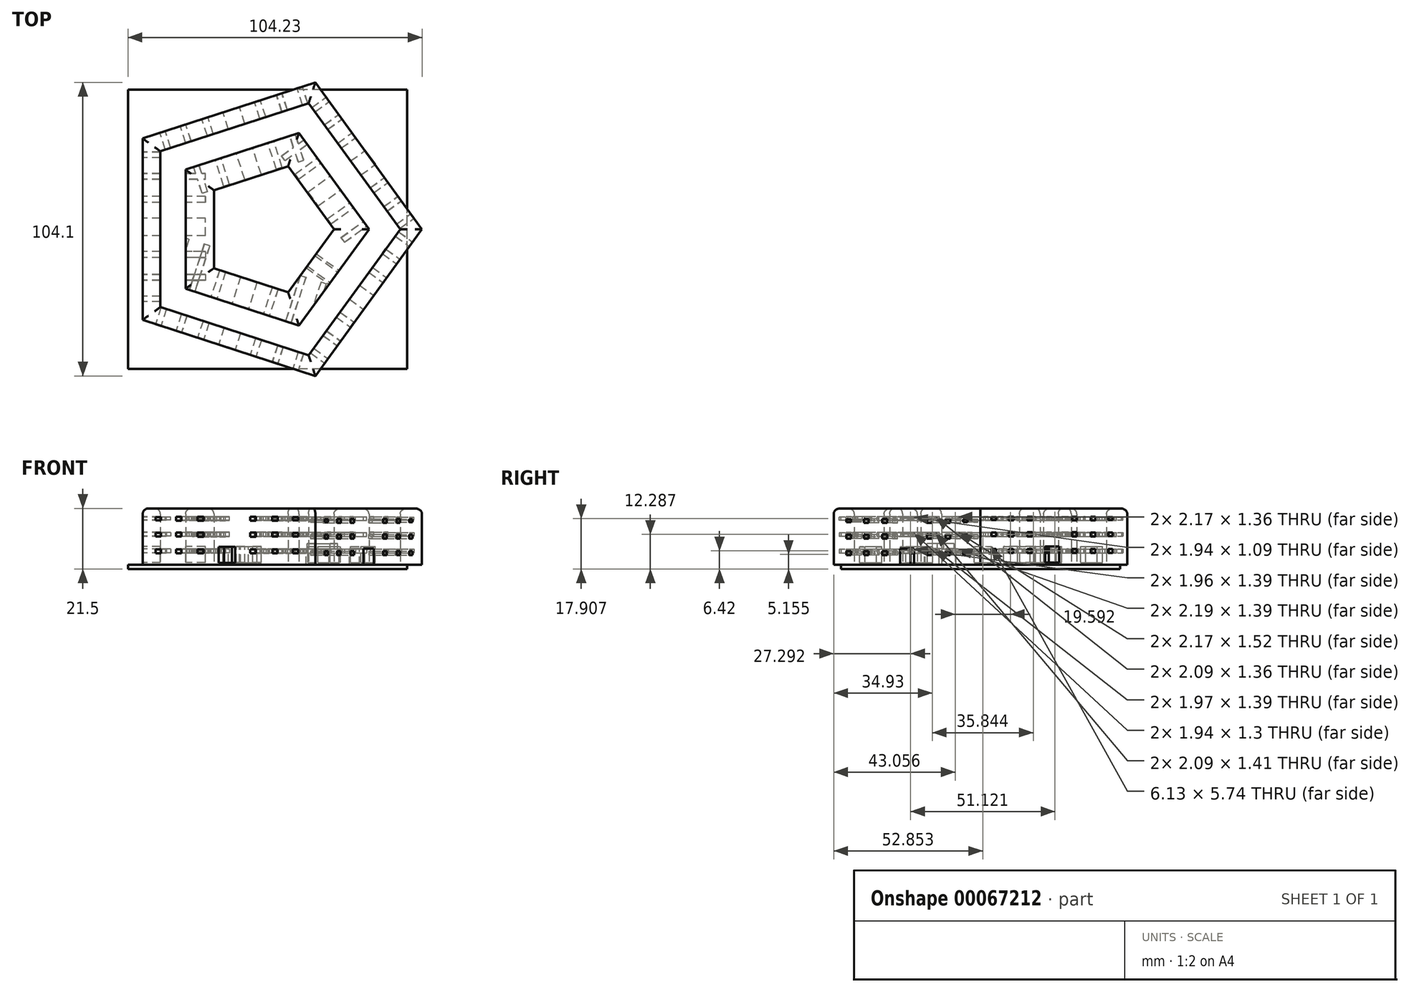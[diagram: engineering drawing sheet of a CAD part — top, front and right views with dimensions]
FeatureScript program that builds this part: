
annotation { "Feature Type Name" : "Feature", "Feature Type Description" : "" }
export const myFeature = defineFeature(function(context is Context, id is Id, definition is map)
    precondition{}
    {
        {
            var Q0;
            Q0=qCreatedBy(makeId("Top.planeOp"),FACE);
            var sketch = newSketch(context, id + "F0", { "sketchPlane" : qUnion([Q0])});
            skCircle(sketch, "E0.cCircle", {"center": v(0, 0) * mm, "radius": 46.99 * mm});
            skLineSegment(sketch, "E0.0", {"start": v(46.99, 0) * mm, "end": v(14.52, -44.69) * mm});
            skLineSegment(sketch, "E0.1", {"start": v(14.52, -44.69) * mm, "end": v(-38.01, -27.62) * mm});
            skLineSegment(sketch, "E0.2", {"start": v(-38.01, -27.62) * mm, "end": v(-38.01, 27.62) * mm});
            skLineSegment(sketch, "E0.3", {"start": v(-38.01, 27.62) * mm, "end": v(14.52, 44.69) * mm});
            skLineSegment(sketch, "E0.4", {"start": v(14.52, 44.69) * mm, "end": v(46.99, 0) * mm});
            skCircle(sketch, "E1.cCircle", {"center": v(0, 0) * mm, "radius": 35.93 * mm, "construction": true});
            skLineSegment(sketch, "E1.0", {"start": v(35.93, 0) * mm, "end": v(11.1, -34.17) * mm});
            skLineSegment(sketch, "E1.1", {"start": v(11.1, -34.17) * mm, "end": v(-29.07, -21.12) * mm});
            skLineSegment(sketch, "E1.2", {"start": v(-29.07, -21.12) * mm, "end": v(-29.07, 21.12) * mm});
            skLineSegment(sketch, "E1.3", {"start": v(-29.07, 21.12) * mm, "end": v(11.1, 34.17) * mm});
            skLineSegment(sketch, "E1.4", {"start": v(11.1, 34.17) * mm, "end": v(35.93, 0) * mm});
            skCircle(sketch, "E2.cCircle", {"center": v(0, 0) * mm, "radius": 23.52 * mm, "construction": true});
            skPoint(sketch, "E2.cCircle.perimeterSnap0", {"position": v(23.52, -17.09) * mm});
            skLineSegment(sketch, "E2.0", {"start": v(23.52, 0) * mm, "end": v(7.27, -22.37) * mm});
            skPoint(sketch, "E2.0.startSnap0", {"position": v(23.52, -17.09) * mm});
            skLineSegment(sketch, "E2.1", {"start": v(7.27, -22.37) * mm, "end": v(-19.03, -13.82) * mm});
            skLineSegment(sketch, "E2.2", {"start": v(-19.03, -13.82) * mm, "end": v(-19.03, 13.82) * mm});
            skLineSegment(sketch, "E2.3", {"start": v(-19.03, 13.82) * mm, "end": v(7.27, 22.37) * mm});
            skLineSegment(sketch, "E2.4", {"start": v(7.27, 22.37) * mm, "end": v(23.52, 0) * mm});
            skCircle(sketch, "E3.cCircle", {"center": v(0, 0) * mm, "radius": 54.73 * mm, "construction": true});
            skLineSegment(sketch, "E3.0", {"start": v(54.73, 0) * mm, "end": v(16.91, -52.05) * mm});
            skLineSegment(sketch, "E3.1", {"start": v(16.91, -52.05) * mm, "end": v(-44.27, -32.17) * mm});
            skLineSegment(sketch, "E3.2", {"start": v(-44.27, -32.17) * mm, "end": v(-44.27, 32.17) * mm});
            skLineSegment(sketch, "E3.3", {"start": v(-44.27, 32.17) * mm, "end": v(16.91, 52.05) * mm});
            skLineSegment(sketch, "E3.4", {"start": v(16.91, 52.05) * mm, "end": v(54.73, 0) * mm});
            skSolve(sketch);
        }
        {
            var Q0;
            Q0=makeQuery(id+"F0.imprint","IMPRINT",FACE,{"disambiguationData":[TD([[makeQuery(id+"F0.imprint","IMPRINT",EDGE,{"derivedFrom":sQuery(id+"F0.wireOp",EDGE,"E1.0")}),-1.0]])]});
            var Q1;
            {var subQ0=sQuery(id+"F0.wireOp",EDGE,"E0.0");Q1=makeQuery(id+"F0.imprint","IMPRINT",FACE,{"disambiguationData":[TD([[makeQuery(id+"F0.imprint","IMPRINT",EDGE,{"derivedFrom":subQ0}),1.0]])]});}
            var Q2;
            {var subQ2=sQuery(id+"F0.wireOp",EDGE,"E3.4");var subQ4=sQuery(id+"F0.wireOp",EDGE,"E3.0");var subQ6=makeQuery(id+"F0.imprint","INTERSECT",VERTEX,{"derivedFrom":[subQ4,subQ2]});Q2=makeQuery(id+"F0.imprint","IMPRINT",FACE,{"disambiguationData":[TD([[makeQuery(id+"F0.imprint","IMPRINT",EDGE,{"disambiguationData":[TD([[subQ6,-1.0]])],"derivedFrom":subQ4}),-1.0]])]});}
            var Q3;
            {var subQ0=sQuery(id+"F0.wireOp",EDGE,"E0.4");Q3=makeQuery(id+"F0.imprint","IMPRINT",FACE,{"disambiguationData":[TD([[makeQuery(id+"F0.imprint","IMPRINT",EDGE,{"derivedFrom":subQ0}),1.0]])]});}
            var Q4;
            {var subQ2=sQuery(id+"F0.wireOp",EDGE,"E3.4");var subQ4=sQuery(id+"F0.wireOp",EDGE,"E3.3");var subQ6=makeQuery(id+"F0.imprint","INTERSECT",VERTEX,{"derivedFrom":[subQ4,subQ2]});Q4=makeQuery(id+"F0.imprint","IMPRINT",FACE,{"disambiguationData":[TD([[makeQuery(id+"F0.imprint","IMPRINT",EDGE,{"disambiguationData":[TD([[subQ6,1.0]])],"derivedFrom":subQ4}),-1.0]])]});}
            var Q5;
            {var subQ0=sQuery(id+"F0.wireOp",EDGE,"E0.3");Q5=makeQuery(id+"F0.imprint","IMPRINT",FACE,{"disambiguationData":[TD([[makeQuery(id+"F0.imprint","IMPRINT",EDGE,{"derivedFrom":subQ0}),1.0]])]});}
            var Q6;
            {var subQ0=sQuery(id+"F0.wireOp",EDGE,"E0.2");Q6=makeQuery(id+"F0.imprint","IMPRINT",FACE,{"disambiguationData":[TD([[makeQuery(id+"F0.imprint","IMPRINT",EDGE,{"derivedFrom":subQ0}),1.0]])]});}
            var Q7;
            {var subQ2=sQuery(id+"F0.wireOp",EDGE,"E3.3");var subQ4=sQuery(id+"F0.wireOp",EDGE,"E3.2");var subQ6=makeQuery(id+"F0.imprint","INTERSECT",VERTEX,{"derivedFrom":[subQ4,subQ2]});Q7=makeQuery(id+"F0.imprint","IMPRINT",FACE,{"disambiguationData":[TD([[makeQuery(id+"F0.imprint","IMPRINT",EDGE,{"disambiguationData":[TD([[subQ6,1.0]])],"derivedFrom":subQ4}),-1.0]])]});}
            var Q8;
            {var subQ0=sQuery(id+"F0.wireOp",EDGE,"E0.1");Q8=makeQuery(id+"F0.imprint","IMPRINT",FACE,{"disambiguationData":[TD([[makeQuery(id+"F0.imprint","IMPRINT",EDGE,{"derivedFrom":subQ0}),1.0]])]});}
            var Q9;
            {var subQ2=sQuery(id+"F0.wireOp",EDGE,"E3.1");var subQ4=sQuery(id+"F0.wireOp",EDGE,"E3.0");var subQ6=makeQuery(id+"F0.imprint","INTERSECT",VERTEX,{"derivedFrom":[subQ4,subQ2]});Q9=makeQuery(id+"F0.imprint","IMPRINT",FACE,{"disambiguationData":[TD([[makeQuery(id+"F0.imprint","IMPRINT",EDGE,{"disambiguationData":[TD([[subQ6,1.0]])],"derivedFrom":subQ4}),-1.0]])]});}
            var Q10;
            {var subQ2=sQuery(id+"F0.wireOp",EDGE,"E3.2");var subQ4=sQuery(id+"F0.wireOp",EDGE,"E3.1");var subQ6=makeQuery(id+"F0.imprint","INTERSECT",VERTEX,{"derivedFrom":[subQ4,subQ2]});Q10=makeQuery(id+"F0.imprint","IMPRINT",FACE,{"disambiguationData":[TD([[makeQuery(id+"F0.imprint","IMPRINT",EDGE,{"disambiguationData":[TD([[subQ6,1.0]])],"derivedFrom":subQ4}),-1.0]])]});}
            extrude(context, id + "F1", {"entities" : qUnion([Q0, Q1, Q2, Q3, Q4, Q5, Q6, Q7, Q8, Q9, Q10]), "depth" : 20 * mm});
        }
        {
            var Q0;
            Q0=makeQuery(id+"F1.opExtrude","SWEPT_FACE",FACE,{"disambiguationData":[OSD([sQuery(id+"F0.wireOp",EDGE,"E3.0")])]});
            var sketch = newSketch(context, id + "F2", { "sketchPlane" : qUnion([Q0])});
            skLineSegment(sketch, "E4.bottom", {"start": v(0, 0) * mm, "end": v(-3.07, 0) * mm});
            skLineSegment(sketch, "E4.top", {"start": v(0, 5.74) * mm, "end": v(-3.07, 5.74) * mm});
            skLineSegment(sketch, "E4.left", {"start": v(0, 0) * mm, "end": v(0, 5.74) * mm});
            skLineSegment(sketch, "E4.right", {"start": v(-3.07, 0) * mm, "end": v(-3.07, 5.74) * mm});
            skLineSegment(sketch, "E5.rect.bottom", {"start": v(-24.6, 15.07) * mm, "end": v(-26.53, 15.07) * mm});
            skLineSegment(sketch, "E5.rect.top", {"start": v(-24.6, 16.17) * mm, "end": v(-26.53, 16.17) * mm});
            skLineSegment(sketch, "E5.rect.left", {"start": v(-24.6, 15.07) * mm, "end": v(-24.6, 16.17) * mm});
            skLineSegment(sketch, "E5.rect.right", {"start": v(-26.53, 15.07) * mm, "end": v(-26.53, 16.17) * mm});
            skPoint(sketch, "E5.rect.middle", {"position": v(-25.56, 15.62) * mm});
            skLineSegment(sketch, "E6.rect.bottom", {"start": v(-24.6, 10.65) * mm, "end": v(-26.53, 10.65) * mm});
            skLineSegment(sketch, "E6.rect.top", {"start": v(-24.6, 9.35) * mm, "end": v(-26.53, 9.35) * mm});
            skLineSegment(sketch, "E6.rect.left", {"start": v(-24.6, 10.65) * mm, "end": v(-24.6, 9.35) * mm});
            skLineSegment(sketch, "E6.rect.right", {"start": v(-26.53, 10.65) * mm, "end": v(-26.53, 9.35) * mm});
            skPoint(sketch, "E6.rect.middle", {"position": v(-25.56, 10) * mm});
            skLineSegment(sketch, "E7.rect.bottom", {"start": v(-24.58, 4.83) * mm, "end": v(-26.54, 4.83) * mm});
            skLineSegment(sketch, "E7.rect.top", {"start": v(-24.58, 3.44) * mm, "end": v(-26.54, 3.44) * mm});
            skLineSegment(sketch, "E7.rect.left", {"start": v(-24.58, 4.83) * mm, "end": v(-24.58, 3.44) * mm});
            skLineSegment(sketch, "E7.rect.right", {"start": v(-26.54, 4.83) * mm, "end": v(-26.54, 3.44) * mm});
            skPoint(sketch, "E7.rect.middle", {"position": v(-25.56, 4.13) * mm});
            skLineSegment(sketch, "E8.rect.bottom", {"start": v(-16.94, 4.83) * mm, "end": v(-18.9, 4.83) * mm});
            skLineSegment(sketch, "E8.rect.top", {"start": v(-16.94, 3.44) * mm, "end": v(-18.9, 3.44) * mm});
            skLineSegment(sketch, "E8.rect.left", {"start": v(-16.94, 4.83) * mm, "end": v(-16.94, 3.44) * mm});
            skLineSegment(sketch, "E8.rect.right", {"start": v(-18.9, 4.83) * mm, "end": v(-18.9, 3.44) * mm});
            skPoint(sketch, "E8.rect.middle", {"position": v(-17.92, 4.13) * mm});
            skLineSegment(sketch, "E9.rect.bottom", {"start": v(-16.88, 9.3) * mm, "end": v(-18.97, 9.3) * mm});
            skLineSegment(sketch, "E9.rect.top", {"start": v(-16.88, 10.7) * mm, "end": v(-18.97, 10.7) * mm});
            skLineSegment(sketch, "E9.rect.left", {"start": v(-16.88, 9.3) * mm, "end": v(-16.88, 10.7) * mm});
            skLineSegment(sketch, "E9.rect.right", {"start": v(-18.97, 9.3) * mm, "end": v(-18.97, 10.7) * mm});
            skPoint(sketch, "E9.rect.middle", {"position": v(-17.92, 10) * mm});
            skLineSegment(sketch, "E10.rect.bottom", {"start": v(-16.88, 14.94) * mm, "end": v(-18.97, 14.94) * mm});
            skLineSegment(sketch, "E10.rect.top", {"start": v(-16.88, 16.3) * mm, "end": v(-18.97, 16.3) * mm});
            skLineSegment(sketch, "E10.rect.left", {"start": v(-16.88, 14.94) * mm, "end": v(-16.88, 16.3) * mm});
            skLineSegment(sketch, "E10.rect.right", {"start": v(-18.97, 14.94) * mm, "end": v(-18.97, 16.3) * mm});
            skPoint(sketch, "E10.rect.middle", {"position": v(-17.92, 15.62) * mm});
            skLineSegment(sketch, "E11.rect.bottom", {"start": v(-10.88, 14.94) * mm, "end": v(-8.71, 14.94) * mm});
            skLineSegment(sketch, "E11.rect.top", {"start": v(-10.88, 16.3) * mm, "end": v(-8.71, 16.3) * mm});
            skLineSegment(sketch, "E11.rect.left", {"start": v(-10.88, 14.94) * mm, "end": v(-10.88, 16.3) * mm});
            skLineSegment(sketch, "E11.rect.right", {"start": v(-8.71, 14.94) * mm, "end": v(-8.71, 16.3) * mm});
            skPoint(sketch, "E11.rect.middle", {"position": v(-9.8, 15.62) * mm});
            skLineSegment(sketch, "E12.rect.bottom", {"start": v(-10.88, 9.24) * mm, "end": v(-8.71, 9.24) * mm});
            skLineSegment(sketch, "E12.rect.top", {"start": v(-10.88, 10.76) * mm, "end": v(-8.71, 10.76) * mm});
            skLineSegment(sketch, "E12.rect.left", {"start": v(-10.88, 9.24) * mm, "end": v(-10.88, 10.76) * mm});
            skLineSegment(sketch, "E12.rect.right", {"start": v(-8.71, 9.24) * mm, "end": v(-8.71, 10.76) * mm});
            skPoint(sketch, "E12.rect.middle", {"position": v(-9.8, 10) * mm});
            skLineSegment(sketch, "E13.rect.bottom", {"start": v(-8.7, 4.83) * mm, "end": v(-10.89, 4.83) * mm});
            skLineSegment(sketch, "E13.rect.top", {"start": v(-8.7, 3.44) * mm, "end": v(-10.89, 3.44) * mm});
            skLineSegment(sketch, "E13.rect.left", {"start": v(-8.7, 4.83) * mm, "end": v(-8.7, 3.44) * mm});
            skLineSegment(sketch, "E13.rect.right", {"start": v(-10.89, 4.83) * mm, "end": v(-10.89, 3.44) * mm});
            skPoint(sketch, "E13.rect.middle", {"position": v(-9.8, 4.13) * mm});
            skLineSegment(sketch, "E14.MirrorCS", {"start": v(3.07, 0) * mm, "end": v(3.07, 5.74) * mm});
            skLineSegment(sketch, "E15.MirrorCS", {"start": v(0, 5.74) * mm, "end": v(3.07, 5.74) * mm});
            skLineSegment(sketch, "E16.MirrorCS", {"start": v(8.7, 4.83) * mm, "end": v(8.7, 3.44) * mm});
            skLineSegment(sketch, "E17.MirrorCS", {"start": v(8.7, 4.83) * mm, "end": v(10.89, 4.83) * mm});
            skLineSegment(sketch, "E18.MirrorCS", {"start": v(10.89, 4.83) * mm, "end": v(10.89, 3.44) * mm});
            skLineSegment(sketch, "E19.MirrorCS", {"start": v(8.7, 3.44) * mm, "end": v(10.89, 3.44) * mm});
            skLineSegment(sketch, "E20.MirrorCS", {"start": v(8.71, 9.24) * mm, "end": v(8.71, 10.76) * mm});
            skLineSegment(sketch, "E21.MirrorCS", {"start": v(10.88, 10.76) * mm, "end": v(8.71, 10.76) * mm});
            skLineSegment(sketch, "E22.MirrorCS", {"start": v(10.88, 9.24) * mm, "end": v(10.88, 10.76) * mm});
            skLineSegment(sketch, "E23.MirrorCS", {"start": v(10.88, 9.24) * mm, "end": v(8.71, 9.24) * mm});
            skLineSegment(sketch, "E24.MirrorCS", {"start": v(10.88, 16.3) * mm, "end": v(8.71, 16.3) * mm});
            skLineSegment(sketch, "E25.MirrorCS", {"start": v(8.71, 14.94) * mm, "end": v(8.71, 16.3) * mm});
            skLineSegment(sketch, "E26.MirrorCS", {"start": v(10.88, 14.94) * mm, "end": v(8.71, 14.94) * mm});
            skLineSegment(sketch, "E27.MirrorCS", {"start": v(10.88, 14.94) * mm, "end": v(10.88, 16.3) * mm});
            skLineSegment(sketch, "E28.MirrorCS", {"start": v(16.88, 14.94) * mm, "end": v(16.88, 16.3) * mm});
            skLineSegment(sketch, "E29.MirrorCS", {"start": v(16.88, 16.3) * mm, "end": v(18.97, 16.3) * mm});
            skLineSegment(sketch, "E30.MirrorCS", {"start": v(18.97, 14.94) * mm, "end": v(18.97, 16.3) * mm});
            skLineSegment(sketch, "E31.MirrorCS", {"start": v(16.88, 14.94) * mm, "end": v(18.97, 14.94) * mm});
            skLineSegment(sketch, "E32.MirrorCS", {"start": v(16.88, 10.7) * mm, "end": v(18.97, 10.7) * mm});
            skLineSegment(sketch, "E33.MirrorCS", {"start": v(16.88, 9.3) * mm, "end": v(16.88, 10.7) * mm});
            skLineSegment(sketch, "E34.MirrorCS", {"start": v(16.88, 9.3) * mm, "end": v(18.97, 9.3) * mm});
            skLineSegment(sketch, "E35.MirrorCS", {"start": v(18.97, 9.3) * mm, "end": v(18.97, 10.7) * mm});
            skLineSegment(sketch, "E36.MirrorCS", {"start": v(24.6, 15.07) * mm, "end": v(24.6, 16.17) * mm});
            skPoint(sketch, "E37.MirrorP", {"position": v(25.56, 15.62) * mm});
            skLineSegment(sketch, "E38.MirrorCS", {"start": v(24.6, 16.17) * mm, "end": v(26.53, 16.17) * mm});
            skLineSegment(sketch, "E39.MirrorCS", {"start": v(26.53, 15.07) * mm, "end": v(26.53, 16.17) * mm});
            skLineSegment(sketch, "E40.MirrorCS", {"start": v(24.6, 15.07) * mm, "end": v(26.53, 15.07) * mm});
            skLineSegment(sketch, "E41.MirrorCS", {"start": v(24.6, 10.65) * mm, "end": v(26.53, 10.65) * mm});
            skLineSegment(sketch, "E42.MirrorCS", {"start": v(24.6, 10.65) * mm, "end": v(24.6, 9.35) * mm});
            skLineSegment(sketch, "E43.MirrorCS", {"start": v(24.6, 9.35) * mm, "end": v(26.53, 9.35) * mm});
            skLineSegment(sketch, "E44.MirrorCS", {"start": v(26.53, 10.65) * mm, "end": v(26.53, 9.35) * mm});
            skPoint(sketch, "E45.MirrorP", {"position": v(25.56, 4.13) * mm});
            skPoint(sketch, "E46.MirrorP", {"position": v(17.92, 4.13) * mm});
            skPoint(sketch, "E47.MirrorP", {"position": v(9.8, 4.13) * mm});
            skPoint(sketch, "E48.MirrorP", {"position": v(9.8, 10) * mm});
            skPoint(sketch, "E49.MirrorP", {"position": v(9.8, 15.62) * mm});
            skPoint(sketch, "E50.MirrorP", {"position": v(17.92, 15.62) * mm});
            skPoint(sketch, "E51.MirrorP", {"position": v(17.92, 10) * mm});
            skPoint(sketch, "E52.MirrorP", {"position": v(25.56, 10) * mm});
            skLineSegment(sketch, "E53.MirrorCS", {"start": v(16.94, 4.83) * mm, "end": v(18.9, 4.83) * mm});
            skLineSegment(sketch, "E54.MirrorCS", {"start": v(18.9, 4.83) * mm, "end": v(18.9, 3.44) * mm});
            skLineSegment(sketch, "E55.MirrorCS", {"start": v(16.94, 3.44) * mm, "end": v(18.9, 3.44) * mm});
            skLineSegment(sketch, "E56.MirrorCS", {"start": v(16.94, 4.83) * mm, "end": v(16.94, 3.44) * mm});
            skLineSegment(sketch, "E57.MirrorCS", {"start": v(24.58, 4.83) * mm, "end": v(26.54, 4.83) * mm});
            skLineSegment(sketch, "E58.MirrorCS", {"start": v(26.54, 4.83) * mm, "end": v(26.54, 3.44) * mm});
            skLineSegment(sketch, "E59.MirrorCS", {"start": v(24.58, 3.44) * mm, "end": v(26.54, 3.44) * mm});
            skLineSegment(sketch, "E60.MirrorCS", {"start": v(24.58, 4.83) * mm, "end": v(24.58, 3.44) * mm});
            skSolve(sketch);
        }
        {
            var Q0;
            Q0 = qSketchRegion(id + "F2", true);
            extrude(context, id + "F3", {"entities" : qUnion([Q0]), "operationType" : NewBodyOperationType.REMOVE, "oppositeDirection" : true, "depth" : 15 * mm});
        }
        {
            var Q0;
            {var subQ0=sQuery(id+"F2.wireOp",EDGE,"E4.left");Q0=makeQuery(id+"F2.imprint","IMPRINT",FACE,{"disambiguationData":[TD([[makeQuery(id+"F2.imprint","IMPRINT",EDGE,{"derivedFrom":subQ0}),-1.0]])]});}
            var Q1;
            Q1=makeQuery(id+"F2.imprint","IMPRINT",FACE,{"disambiguationData":[TD([[makeQuery(id+"F2.imprint","IMPRINT",EDGE,{"derivedFrom":sQuery(id+"F2.wireOp",EDGE,"E4.bottom")}),-1.0]])]});
            extrude(context, id + "F4", {"entities" : qUnion([Q0, Q1]), "operationType" : NewBodyOperationType.REMOVE, "oppositeDirection" : true, "depth" : 61.4 * mm});
        }
        {
            var Q0;
            Q0=makeQuery(id+"F1.opExtrude","SWEPT_FACE",FACE,{"disambiguationData":[OSD([sQuery(id+"F0.wireOp",EDGE,"E1.0")])]});
            var sketch = newSketch(context, id + "F5", { "sketchPlane" : qUnion([Q0])});
            skLineSegment(sketch, "E61.bottom", {"start": v(0, 0) * mm, "end": v(-2.3, 0) * mm});
            skLineSegment(sketch, "E61.top", {"start": v(0, 7.45) * mm, "end": v(-2.3, 7.45) * mm});
            skLineSegment(sketch, "E61.left", {"start": v(0, 0) * mm, "end": v(0, 7.45) * mm});
            skLineSegment(sketch, "E61.right", {"start": v(-2.3, 0) * mm, "end": v(-2.3, 7.45) * mm});
            skLineSegment(sketch, "E62.MirrorCS", {"start": v(0, 7.45) * mm, "end": v(2.3, 7.45) * mm});
            skLineSegment(sketch, "E63.MirrorCS", {"start": v(2.3, 0) * mm, "end": v(2.3, 7.45) * mm});
            skLineSegment(sketch, "E64.MirrorCS", {"start": v(0, 0) * mm, "end": v(2.3, 0) * mm});
            skSolve(sketch);
        }
        {
            var Q0;
            Q0 = qSketchRegion(id + "F5", true);
            extrude(context, id + "F6", {"entities" : qUnion([Q0]), "operationType" : NewBodyOperationType.REMOVE, "oppositeDirection" : true, "depth" : 25 * mm});
        }
        {
            var Q0;
            Q0=makeQuery(id+"F1.opExtrude","SWEPT_FACE",FACE,{"disambiguationData":[OSD([sQuery(id+"F0.wireOp",EDGE,"E3.1")])]});
            var sketch = newSketch(context, id + "F7", { "sketchPlane" : qUnion([Q0])});
            skLineSegment(sketch, "E65.bottom", {"start": v(-0.8, 0.7) * mm, "end": v(-3.86, 0.7) * mm});
            skLineSegment(sketch, "E65.top", {"start": v(-0.8, 6.43) * mm, "end": v(-3.86, 6.43) * mm});
            skLineSegment(sketch, "E65.left", {"start": v(-0.8, 0.7) * mm, "end": v(-0.8, 6.43) * mm});
            skLineSegment(sketch, "E65.right", {"start": v(-3.86, 0.7) * mm, "end": v(-3.86, 6.43) * mm});
            skLineSegment(sketch, "E66.rect.bottom", {"start": v(-25.39, 15.77) * mm, "end": v(-27.33, 15.77) * mm});
            skLineSegment(sketch, "E66.rect.top", {"start": v(-25.39, 16.86) * mm, "end": v(-27.33, 16.86) * mm});
            skLineSegment(sketch, "E66.rect.left", {"start": v(-25.39, 15.77) * mm, "end": v(-25.39, 16.86) * mm});
            skLineSegment(sketch, "E66.rect.right", {"start": v(-27.33, 15.77) * mm, "end": v(-27.33, 16.86) * mm});
            skPoint(sketch, "E66.rect.middle", {"position": v(-26.36, 16.32) * mm});
            skLineSegment(sketch, "E67.rect.bottom", {"start": v(-25.39, 11.35) * mm, "end": v(-27.33, 11.35) * mm});
            skLineSegment(sketch, "E67.rect.top", {"start": v(-25.39, 10.05) * mm, "end": v(-27.33, 10.05) * mm});
            skLineSegment(sketch, "E67.rect.left", {"start": v(-25.39, 11.35) * mm, "end": v(-25.39, 10.05) * mm});
            skLineSegment(sketch, "E67.rect.right", {"start": v(-27.33, 11.35) * mm, "end": v(-27.33, 10.05) * mm});
            skPoint(sketch, "E67.rect.middle", {"position": v(-26.36, 10.7) * mm});
            skLineSegment(sketch, "E68.rect.bottom", {"start": v(-25.38, 5.52) * mm, "end": v(-27.34, 5.52) * mm});
            skLineSegment(sketch, "E68.rect.top", {"start": v(-25.38, 4.13) * mm, "end": v(-27.34, 4.13) * mm});
            skLineSegment(sketch, "E68.rect.left", {"start": v(-25.38, 5.52) * mm, "end": v(-25.38, 4.13) * mm});
            skLineSegment(sketch, "E68.rect.right", {"start": v(-27.34, 5.52) * mm, "end": v(-27.34, 4.13) * mm});
            skPoint(sketch, "E68.rect.middle", {"position": v(-26.36, 4.83) * mm});
            skLineSegment(sketch, "E69.rect.bottom", {"start": v(-17.73, 5.52) * mm, "end": v(-19.7, 5.52) * mm});
            skLineSegment(sketch, "E69.rect.top", {"start": v(-17.73, 4.13) * mm, "end": v(-19.7, 4.13) * mm});
            skLineSegment(sketch, "E69.rect.left", {"start": v(-17.73, 5.52) * mm, "end": v(-17.73, 4.13) * mm});
            skLineSegment(sketch, "E69.rect.right", {"start": v(-19.7, 5.52) * mm, "end": v(-19.7, 4.13) * mm});
            skPoint(sketch, "E69.rect.middle", {"position": v(-18.72, 4.83) * mm});
            skLineSegment(sketch, "E70.rect.bottom", {"start": v(-17.67, 10) * mm, "end": v(-19.76, 10) * mm});
            skLineSegment(sketch, "E70.rect.top", {"start": v(-17.67, 11.4) * mm, "end": v(-19.76, 11.4) * mm});
            skLineSegment(sketch, "E70.rect.left", {"start": v(-17.67, 10) * mm, "end": v(-17.67, 11.4) * mm});
            skLineSegment(sketch, "E70.rect.right", {"start": v(-19.76, 10) * mm, "end": v(-19.76, 11.4) * mm});
            skPoint(sketch, "E70.rect.middle", {"position": v(-18.72, 10.7) * mm});
            skLineSegment(sketch, "E71.rect.bottom", {"start": v(-17.67, 15.64) * mm, "end": v(-19.76, 15.64) * mm});
            skLineSegment(sketch, "E71.rect.top", {"start": v(-17.67, 17) * mm, "end": v(-19.76, 17) * mm});
            skLineSegment(sketch, "E71.rect.left", {"start": v(-17.67, 15.64) * mm, "end": v(-17.67, 17) * mm});
            skLineSegment(sketch, "E71.rect.right", {"start": v(-19.76, 15.64) * mm, "end": v(-19.76, 17) * mm});
            skPoint(sketch, "E71.rect.middle", {"position": v(-18.72, 16.32) * mm});
            skLineSegment(sketch, "E72.rect.bottom", {"start": v(-11.67, 15.64) * mm, "end": v(-9.5, 15.64) * mm});
            skLineSegment(sketch, "E72.rect.top", {"start": v(-11.67, 17) * mm, "end": v(-9.5, 17) * mm});
            skLineSegment(sketch, "E72.rect.left", {"start": v(-11.67, 15.64) * mm, "end": v(-11.67, 17) * mm});
            skLineSegment(sketch, "E72.rect.right", {"start": v(-9.5, 15.64) * mm, "end": v(-9.5, 17) * mm});
            skPoint(sketch, "E72.rect.middle", {"position": v(-10.6, 16.32) * mm});
            skLineSegment(sketch, "E73.rect.bottom", {"start": v(-11.67, 9.93) * mm, "end": v(-9.5, 9.93) * mm});
            skLineSegment(sketch, "E73.rect.top", {"start": v(-11.67, 11.46) * mm, "end": v(-9.5, 11.46) * mm});
            skLineSegment(sketch, "E73.rect.left", {"start": v(-11.67, 9.93) * mm, "end": v(-11.67, 11.46) * mm});
            skLineSegment(sketch, "E73.rect.right", {"start": v(-9.5, 9.93) * mm, "end": v(-9.5, 11.46) * mm});
            skPoint(sketch, "E73.rect.middle", {"position": v(-10.6, 10.7) * mm});
            skLineSegment(sketch, "E74.rect.bottom", {"start": v(-9.5, 5.52) * mm, "end": v(-11.68, 5.52) * mm});
            skLineSegment(sketch, "E74.rect.top", {"start": v(-9.5, 4.13) * mm, "end": v(-11.68, 4.13) * mm});
            skLineSegment(sketch, "E74.rect.left", {"start": v(-9.5, 5.52) * mm, "end": v(-9.5, 4.13) * mm});
            skLineSegment(sketch, "E74.rect.right", {"start": v(-11.68, 5.52) * mm, "end": v(-11.68, 4.13) * mm});
            skPoint(sketch, "E74.rect.middle", {"position": v(-10.6, 4.83) * mm});
            skLineSegment(sketch, "E75.MirrorCS", {"start": v(2.27, 0.7) * mm, "end": v(2.27, 6.43) * mm});
            skLineSegment(sketch, "E76.MirrorCS", {"start": v(-0.8, 6.43) * mm, "end": v(2.27, 6.43) * mm});
            skLineSegment(sketch, "E77.MirrorCS", {"start": v(7.9, 5.52) * mm, "end": v(7.9, 4.13) * mm});
            skLineSegment(sketch, "E78.MirrorCS", {"start": v(7.9, 5.52) * mm, "end": v(10.1, 5.52) * mm});
            skLineSegment(sketch, "E79.MirrorCS", {"start": v(10.1, 5.52) * mm, "end": v(10.1, 4.13) * mm});
            skLineSegment(sketch, "E80.MirrorCS", {"start": v(7.9, 4.13) * mm, "end": v(10.1, 4.13) * mm});
            skLineSegment(sketch, "E81.MirrorCS", {"start": v(7.92, 9.93) * mm, "end": v(7.92, 11.46) * mm});
            skLineSegment(sketch, "E82.MirrorCS", {"start": v(10.08, 11.46) * mm, "end": v(7.92, 11.46) * mm});
            skLineSegment(sketch, "E83.MirrorCS", {"start": v(10.08, 9.93) * mm, "end": v(10.08, 11.46) * mm});
            skLineSegment(sketch, "E84.MirrorCS", {"start": v(10.08, 9.93) * mm, "end": v(7.92, 9.93) * mm});
            skLineSegment(sketch, "E85.MirrorCS", {"start": v(10.08, 17) * mm, "end": v(7.92, 17) * mm});
            skLineSegment(sketch, "E86.MirrorCS", {"start": v(7.92, 15.64) * mm, "end": v(7.92, 17) * mm});
            skLineSegment(sketch, "E87.MirrorCS", {"start": v(10.08, 15.64) * mm, "end": v(7.92, 15.64) * mm});
            skLineSegment(sketch, "E88.MirrorCS", {"start": v(10.08, 15.64) * mm, "end": v(10.08, 17) * mm});
            skLineSegment(sketch, "E89.MirrorCS", {"start": v(16.08, 15.64) * mm, "end": v(16.08, 17) * mm});
            skLineSegment(sketch, "E90.MirrorCS", {"start": v(16.08, 17) * mm, "end": v(18.17, 17) * mm});
            skLineSegment(sketch, "E91.MirrorCS", {"start": v(18.17, 15.64) * mm, "end": v(18.17, 17) * mm});
            skLineSegment(sketch, "E92.MirrorCS", {"start": v(16.08, 15.64) * mm, "end": v(18.17, 15.64) * mm});
            skLineSegment(sketch, "E93.MirrorCS", {"start": v(16.08, 11.4) * mm, "end": v(18.17, 11.4) * mm});
            skLineSegment(sketch, "E94.MirrorCS", {"start": v(16.08, 10) * mm, "end": v(16.08, 11.4) * mm});
            skLineSegment(sketch, "E95.MirrorCS", {"start": v(16.08, 10) * mm, "end": v(18.17, 10) * mm});
            skLineSegment(sketch, "E96.MirrorCS", {"start": v(18.17, 10) * mm, "end": v(18.17, 11.4) * mm});
            skLineSegment(sketch, "E97.MirrorCS", {"start": v(23.8, 15.77) * mm, "end": v(23.8, 16.86) * mm});
            skPoint(sketch, "E98.MirrorP", {"position": v(24.77, 16.32) * mm});
            skLineSegment(sketch, "E99.MirrorCS", {"start": v(23.8, 16.86) * mm, "end": v(25.74, 16.86) * mm});
            skLineSegment(sketch, "E100.MirrorCS", {"start": v(25.74, 15.77) * mm, "end": v(25.74, 16.86) * mm});
            skLineSegment(sketch, "E101.MirrorCS", {"start": v(23.8, 15.77) * mm, "end": v(25.74, 15.77) * mm});
            skLineSegment(sketch, "E102.MirrorCS", {"start": v(23.8, 11.35) * mm, "end": v(25.74, 11.35) * mm});
            skLineSegment(sketch, "E103.MirrorCS", {"start": v(23.8, 11.35) * mm, "end": v(23.8, 10.05) * mm});
            skLineSegment(sketch, "E104.MirrorCS", {"start": v(23.8, 10.05) * mm, "end": v(25.74, 10.05) * mm});
            skLineSegment(sketch, "E105.MirrorCS", {"start": v(25.74, 11.35) * mm, "end": v(25.74, 10.05) * mm});
            skPoint(sketch, "E106.MirrorP", {"position": v(24.77, 4.83) * mm});
            skPoint(sketch, "E107.MirrorP", {"position": v(17.13, 4.83) * mm});
            skPoint(sketch, "E108.MirrorP", {"position": v(9, 4.83) * mm});
            skPoint(sketch, "E109.MirrorP", {"position": v(9, 10.7) * mm});
            skPoint(sketch, "E110.MirrorP", {"position": v(9, 16.32) * mm});
            skPoint(sketch, "E111.MirrorP", {"position": v(17.13, 16.32) * mm});
            skPoint(sketch, "E112.MirrorP", {"position": v(17.13, 10.7) * mm});
            skPoint(sketch, "E113.MirrorP", {"position": v(24.77, 10.7) * mm});
            skLineSegment(sketch, "E114.MirrorCS", {"start": v(16.14, 5.52) * mm, "end": v(18.11, 5.52) * mm});
            skLineSegment(sketch, "E115.MirrorCS", {"start": v(18.11, 5.52) * mm, "end": v(18.11, 4.13) * mm});
            skLineSegment(sketch, "E116.MirrorCS", {"start": v(16.14, 4.13) * mm, "end": v(18.11, 4.13) * mm});
            skLineSegment(sketch, "E117.MirrorCS", {"start": v(16.14, 5.52) * mm, "end": v(16.14, 4.13) * mm});
            skLineSegment(sketch, "E118.MirrorCS", {"start": v(23.78, 5.52) * mm, "end": v(25.75, 5.52) * mm});
            skLineSegment(sketch, "E119.MirrorCS", {"start": v(25.75, 5.52) * mm, "end": v(25.75, 4.13) * mm});
            skLineSegment(sketch, "E120.MirrorCS", {"start": v(23.78, 4.13) * mm, "end": v(25.75, 4.13) * mm});
            skLineSegment(sketch, "E121.MirrorCS", {"start": v(23.78, 5.52) * mm, "end": v(23.78, 4.13) * mm});
            skLineSegment(sketch, "E122", {"start": v(2.27, 0.7) * mm, "end": v(-0.8, 0.7) * mm});
            skSolve(sketch);
        }
        {
            var Q0;
            Q0=makeQuery(id+"F1.opExtrude","SWEPT_FACE",FACE,{"disambiguationData":[OSD([sQuery(id+"F0.wireOp",EDGE,"E3.2")])]});
            var sketch = newSketch(context, id + "F8", { "sketchPlane" : qUnion([Q0])});
            skLineSegment(sketch, "E123.bottom", {"start": v(-0.8, 0.79) * mm, "end": v(-3.87, 0.79) * mm});
            skLineSegment(sketch, "E123.top", {"start": v(-0.8, 6.52) * mm, "end": v(-3.87, 6.52) * mm});
            skLineSegment(sketch, "E123.left", {"start": v(-0.8, 0.79) * mm, "end": v(-0.8, 6.52) * mm});
            skLineSegment(sketch, "E123.right", {"start": v(-3.87, 0.79) * mm, "end": v(-3.87, 6.52) * mm});
            skLineSegment(sketch, "E124.rect.bottom", {"start": v(-25.4, 15.86) * mm, "end": v(-27.33, 15.86) * mm});
            skLineSegment(sketch, "E124.rect.top", {"start": v(-25.4, 16.95) * mm, "end": v(-27.33, 16.95) * mm});
            skLineSegment(sketch, "E124.rect.left", {"start": v(-25.4, 15.86) * mm, "end": v(-25.4, 16.95) * mm});
            skLineSegment(sketch, "E124.rect.right", {"start": v(-27.33, 15.86) * mm, "end": v(-27.33, 16.95) * mm});
            skPoint(sketch, "E124.rect.middle", {"position": v(-26.36, 16.4) * mm});
            skLineSegment(sketch, "E125.rect.bottom", {"start": v(-25.4, 11.44) * mm, "end": v(-27.33, 11.44) * mm});
            skLineSegment(sketch, "E125.rect.top", {"start": v(-25.4, 10.14) * mm, "end": v(-27.33, 10.14) * mm});
            skLineSegment(sketch, "E125.rect.left", {"start": v(-25.4, 11.44) * mm, "end": v(-25.4, 10.14) * mm});
            skLineSegment(sketch, "E125.rect.right", {"start": v(-27.33, 11.44) * mm, "end": v(-27.33, 10.14) * mm});
            skPoint(sketch, "E125.rect.middle", {"position": v(-26.36, 10.79) * mm});
            skLineSegment(sketch, "E126.rect.bottom", {"start": v(-25.38, 5.61) * mm, "end": v(-27.34, 5.61) * mm});
            skLineSegment(sketch, "E126.rect.top", {"start": v(-25.38, 4.23) * mm, "end": v(-27.34, 4.23) * mm});
            skLineSegment(sketch, "E126.rect.left", {"start": v(-25.38, 5.61) * mm, "end": v(-25.38, 4.23) * mm});
            skLineSegment(sketch, "E126.rect.right", {"start": v(-27.34, 5.61) * mm, "end": v(-27.34, 4.23) * mm});
            skPoint(sketch, "E126.rect.middle", {"position": v(-26.36, 4.92) * mm});
            skLineSegment(sketch, "E127.rect.bottom", {"start": v(-17.74, 5.61) * mm, "end": v(-19.71, 5.61) * mm});
            skLineSegment(sketch, "E127.rect.top", {"start": v(-17.74, 4.23) * mm, "end": v(-19.71, 4.23) * mm});
            skLineSegment(sketch, "E127.rect.left", {"start": v(-17.74, 5.61) * mm, "end": v(-17.74, 4.23) * mm});
            skLineSegment(sketch, "E127.rect.right", {"start": v(-19.71, 5.61) * mm, "end": v(-19.71, 4.23) * mm});
            skPoint(sketch, "E127.rect.middle", {"position": v(-18.72, 4.92) * mm});
            skLineSegment(sketch, "E128.rect.bottom", {"start": v(-17.68, 10.08) * mm, "end": v(-19.77, 10.08) * mm});
            skLineSegment(sketch, "E128.rect.top", {"start": v(-17.68, 11.5) * mm, "end": v(-19.77, 11.5) * mm});
            skLineSegment(sketch, "E128.rect.left", {"start": v(-17.68, 10.08) * mm, "end": v(-17.68, 11.5) * mm});
            skLineSegment(sketch, "E128.rect.right", {"start": v(-19.77, 10.08) * mm, "end": v(-19.77, 11.5) * mm});
            skPoint(sketch, "E128.rect.middle", {"position": v(-18.72, 10.79) * mm});
            skLineSegment(sketch, "E129.rect.bottom", {"start": v(-17.68, 15.73) * mm, "end": v(-19.77, 15.73) * mm});
            skLineSegment(sketch, "E129.rect.top", {"start": v(-17.68, 17.08) * mm, "end": v(-19.77, 17.08) * mm});
            skLineSegment(sketch, "E129.rect.left", {"start": v(-17.68, 15.73) * mm, "end": v(-17.68, 17.08) * mm});
            skLineSegment(sketch, "E129.rect.right", {"start": v(-19.77, 15.73) * mm, "end": v(-19.77, 17.08) * mm});
            skPoint(sketch, "E129.rect.middle", {"position": v(-18.72, 16.4) * mm});
            skLineSegment(sketch, "E130.rect.bottom", {"start": v(-11.68, 15.73) * mm, "end": v(-9.52, 15.73) * mm});
            skLineSegment(sketch, "E130.rect.top", {"start": v(-11.68, 17.08) * mm, "end": v(-9.52, 17.08) * mm});
            skLineSegment(sketch, "E130.rect.left", {"start": v(-11.68, 15.73) * mm, "end": v(-11.68, 17.08) * mm});
            skLineSegment(sketch, "E130.rect.right", {"start": v(-9.52, 15.73) * mm, "end": v(-9.52, 17.08) * mm});
            skPoint(sketch, "E130.rect.middle", {"position": v(-10.6, 16.4) * mm});
            skLineSegment(sketch, "E131.rect.bottom", {"start": v(-11.68, 10.02) * mm, "end": v(-9.52, 10.02) * mm});
            skLineSegment(sketch, "E131.rect.top", {"start": v(-11.68, 11.55) * mm, "end": v(-9.52, 11.55) * mm});
            skLineSegment(sketch, "E131.rect.left", {"start": v(-11.68, 10.02) * mm, "end": v(-11.68, 11.55) * mm});
            skLineSegment(sketch, "E131.rect.right", {"start": v(-9.52, 10.02) * mm, "end": v(-9.52, 11.55) * mm});
            skPoint(sketch, "E131.rect.middle", {"position": v(-10.6, 10.79) * mm});
            skLineSegment(sketch, "E132.rect.bottom", {"start": v(-9.5, 5.61) * mm, "end": v(-11.7, 5.61) * mm});
            skLineSegment(sketch, "E132.rect.top", {"start": v(-9.5, 4.23) * mm, "end": v(-11.7, 4.23) * mm});
            skLineSegment(sketch, "E132.rect.left", {"start": v(-9.5, 5.61) * mm, "end": v(-9.5, 4.23) * mm});
            skLineSegment(sketch, "E132.rect.right", {"start": v(-11.7, 5.61) * mm, "end": v(-11.7, 4.23) * mm});
            skPoint(sketch, "E132.rect.middle", {"position": v(-10.6, 4.92) * mm});
            skLineSegment(sketch, "E133.MirrorCS", {"start": v(2.26, 0.79) * mm, "end": v(2.26, 6.52) * mm});
            skLineSegment(sketch, "E134.MirrorCS", {"start": v(-0.8, 6.52) * mm, "end": v(2.26, 6.52) * mm});
            skLineSegment(sketch, "E135.MirrorCS", {"start": v(7.9, 5.61) * mm, "end": v(7.9, 4.23) * mm});
            skLineSegment(sketch, "E136.MirrorCS", {"start": v(7.9, 5.61) * mm, "end": v(10.09, 5.61) * mm});
            skLineSegment(sketch, "E137.MirrorCS", {"start": v(10.09, 5.61) * mm, "end": v(10.09, 4.23) * mm});
            skLineSegment(sketch, "E138.MirrorCS", {"start": v(7.9, 4.23) * mm, "end": v(10.09, 4.23) * mm});
            skLineSegment(sketch, "E139.MirrorCS", {"start": v(7.91, 10.02) * mm, "end": v(7.91, 11.55) * mm});
            skLineSegment(sketch, "E140.MirrorCS", {"start": v(10.08, 11.55) * mm, "end": v(7.91, 11.55) * mm});
            skLineSegment(sketch, "E141.MirrorCS", {"start": v(10.08, 10.02) * mm, "end": v(10.08, 11.55) * mm});
            skLineSegment(sketch, "E142.MirrorCS", {"start": v(10.08, 10.02) * mm, "end": v(7.91, 10.02) * mm});
            skLineSegment(sketch, "E143.MirrorCS", {"start": v(10.08, 17.08) * mm, "end": v(7.91, 17.08) * mm});
            skLineSegment(sketch, "E144.MirrorCS", {"start": v(7.91, 15.73) * mm, "end": v(7.91, 17.08) * mm});
            skLineSegment(sketch, "E145.MirrorCS", {"start": v(10.08, 15.73) * mm, "end": v(7.91, 15.73) * mm});
            skLineSegment(sketch, "E146.MirrorCS", {"start": v(10.08, 15.73) * mm, "end": v(10.08, 17.08) * mm});
            skLineSegment(sketch, "E147.MirrorCS", {"start": v(16.07, 15.73) * mm, "end": v(16.07, 17.08) * mm});
            skLineSegment(sketch, "E148.MirrorCS", {"start": v(16.07, 17.08) * mm, "end": v(18.16, 17.08) * mm});
            skLineSegment(sketch, "E149.MirrorCS", {"start": v(18.16, 15.73) * mm, "end": v(18.16, 17.08) * mm});
            skLineSegment(sketch, "E150.MirrorCS", {"start": v(16.07, 15.73) * mm, "end": v(18.16, 15.73) * mm});
            skLineSegment(sketch, "E151.MirrorCS", {"start": v(16.07, 11.5) * mm, "end": v(18.16, 11.5) * mm});
            skLineSegment(sketch, "E152.MirrorCS", {"start": v(16.07, 10.08) * mm, "end": v(16.07, 11.5) * mm});
            skLineSegment(sketch, "E153.MirrorCS", {"start": v(16.07, 10.08) * mm, "end": v(18.16, 10.08) * mm});
            skLineSegment(sketch, "E154.MirrorCS", {"start": v(18.16, 10.08) * mm, "end": v(18.16, 11.5) * mm});
            skLineSegment(sketch, "E155.MirrorCS", {"start": v(23.79, 15.86) * mm, "end": v(23.79, 16.95) * mm});
            skPoint(sketch, "E156.MirrorP", {"position": v(24.76, 16.4) * mm});
            skLineSegment(sketch, "E157.MirrorCS", {"start": v(23.79, 16.95) * mm, "end": v(25.73, 16.95) * mm});
            skLineSegment(sketch, "E158.MirrorCS", {"start": v(25.73, 15.86) * mm, "end": v(25.73, 16.95) * mm});
            skLineSegment(sketch, "E159.MirrorCS", {"start": v(23.79, 15.86) * mm, "end": v(25.73, 15.86) * mm});
            skLineSegment(sketch, "E160.MirrorCS", {"start": v(23.79, 11.44) * mm, "end": v(25.73, 11.44) * mm});
            skLineSegment(sketch, "E161.MirrorCS", {"start": v(23.79, 11.44) * mm, "end": v(23.79, 10.14) * mm});
            skLineSegment(sketch, "E162.MirrorCS", {"start": v(23.79, 10.14) * mm, "end": v(25.73, 10.14) * mm});
            skLineSegment(sketch, "E163.MirrorCS", {"start": v(25.73, 11.44) * mm, "end": v(25.73, 10.14) * mm});
            skPoint(sketch, "E164.MirrorP", {"position": v(24.76, 4.92) * mm});
            skPoint(sketch, "E165.MirrorP", {"position": v(17.12, 4.92) * mm});
            skPoint(sketch, "E166.MirrorP", {"position": v(9, 4.92) * mm});
            skPoint(sketch, "E167.MirrorP", {"position": v(9, 10.79) * mm});
            skPoint(sketch, "E168.MirrorP", {"position": v(9, 16.4) * mm});
            skPoint(sketch, "E169.MirrorP", {"position": v(17.12, 16.4) * mm});
            skPoint(sketch, "E170.MirrorP", {"position": v(17.12, 10.79) * mm});
            skPoint(sketch, "E171.MirrorP", {"position": v(24.76, 10.79) * mm});
            skLineSegment(sketch, "E172.MirrorCS", {"start": v(16.13, 5.61) * mm, "end": v(18.1, 5.61) * mm});
            skLineSegment(sketch, "E173.MirrorCS", {"start": v(18.1, 5.61) * mm, "end": v(18.1, 4.23) * mm});
            skLineSegment(sketch, "E174.MirrorCS", {"start": v(16.13, 4.23) * mm, "end": v(18.1, 4.23) * mm});
            skLineSegment(sketch, "E175.MirrorCS", {"start": v(16.13, 5.61) * mm, "end": v(16.13, 4.23) * mm});
            skLineSegment(sketch, "E176.MirrorCS", {"start": v(23.78, 5.61) * mm, "end": v(25.74, 5.61) * mm});
            skLineSegment(sketch, "E177.MirrorCS", {"start": v(25.74, 5.61) * mm, "end": v(25.74, 4.23) * mm});
            skLineSegment(sketch, "E178.MirrorCS", {"start": v(23.78, 4.23) * mm, "end": v(25.74, 4.23) * mm});
            skLineSegment(sketch, "E179.MirrorCS", {"start": v(23.78, 5.61) * mm, "end": v(23.78, 4.23) * mm});
            skLineSegment(sketch, "E180", {"start": v(2.26, 0.79) * mm, "end": v(-0.8, 0.79) * mm});
            skSolve(sketch);
        }
        {
            var Q0;
            Q0=makeQuery(id+"F1.opExtrude","SWEPT_FACE",FACE,{"disambiguationData":[OSD([sQuery(id+"F0.wireOp",EDGE,"E3.3")])]});
            var sketch = newSketch(context, id + "F9", { "sketchPlane" : qUnion([Q0])});
            skLineSegment(sketch, "E181.bottom", {"start": v(-0.8, 0.79) * mm, "end": v(-3.87, 0.79) * mm});
            skLineSegment(sketch, "E181.top", {"start": v(-0.8, 6.52) * mm, "end": v(-3.87, 6.52) * mm});
            skLineSegment(sketch, "E181.left", {"start": v(-0.8, 0.79) * mm, "end": v(-0.8, 6.52) * mm});
            skLineSegment(sketch, "E181.right", {"start": v(-3.87, 0.79) * mm, "end": v(-3.87, 6.52) * mm});
            skLineSegment(sketch, "E182.rect.bottom", {"start": v(-25.4, 15.86) * mm, "end": v(-27.33, 15.86) * mm});
            skLineSegment(sketch, "E182.rect.top", {"start": v(-25.4, 16.95) * mm, "end": v(-27.33, 16.95) * mm});
            skLineSegment(sketch, "E182.rect.left", {"start": v(-25.4, 15.86) * mm, "end": v(-25.4, 16.95) * mm});
            skLineSegment(sketch, "E182.rect.right", {"start": v(-27.33, 15.86) * mm, "end": v(-27.33, 16.95) * mm});
            skPoint(sketch, "E182.rect.middle", {"position": v(-26.36, 16.4) * mm});
            skLineSegment(sketch, "E183.rect.bottom", {"start": v(-25.4, 11.44) * mm, "end": v(-27.33, 11.44) * mm});
            skLineSegment(sketch, "E183.rect.top", {"start": v(-25.4, 10.14) * mm, "end": v(-27.33, 10.14) * mm});
            skLineSegment(sketch, "E183.rect.left", {"start": v(-25.4, 11.44) * mm, "end": v(-25.4, 10.14) * mm});
            skLineSegment(sketch, "E183.rect.right", {"start": v(-27.33, 11.44) * mm, "end": v(-27.33, 10.14) * mm});
            skPoint(sketch, "E183.rect.middle", {"position": v(-26.36, 10.79) * mm});
            skLineSegment(sketch, "E184.rect.bottom", {"start": v(-25.38, 5.61) * mm, "end": v(-27.34, 5.61) * mm});
            skLineSegment(sketch, "E184.rect.top", {"start": v(-25.38, 4.23) * mm, "end": v(-27.34, 4.23) * mm});
            skLineSegment(sketch, "E184.rect.left", {"start": v(-25.38, 5.61) * mm, "end": v(-25.38, 4.23) * mm});
            skLineSegment(sketch, "E184.rect.right", {"start": v(-27.34, 5.61) * mm, "end": v(-27.34, 4.23) * mm});
            skPoint(sketch, "E184.rect.middle", {"position": v(-26.36, 4.92) * mm});
            skLineSegment(sketch, "E185.rect.bottom", {"start": v(-17.74, 5.61) * mm, "end": v(-19.71, 5.61) * mm});
            skLineSegment(sketch, "E185.rect.top", {"start": v(-17.74, 4.23) * mm, "end": v(-19.71, 4.23) * mm});
            skLineSegment(sketch, "E185.rect.left", {"start": v(-17.74, 5.61) * mm, "end": v(-17.74, 4.23) * mm});
            skLineSegment(sketch, "E185.rect.right", {"start": v(-19.71, 5.61) * mm, "end": v(-19.71, 4.23) * mm});
            skPoint(sketch, "E185.rect.middle", {"position": v(-18.72, 4.92) * mm});
            skLineSegment(sketch, "E186.rect.bottom", {"start": v(-17.68, 10.08) * mm, "end": v(-19.77, 10.08) * mm});
            skLineSegment(sketch, "E186.rect.top", {"start": v(-17.68, 11.5) * mm, "end": v(-19.77, 11.5) * mm});
            skLineSegment(sketch, "E186.rect.left", {"start": v(-17.68, 10.08) * mm, "end": v(-17.68, 11.5) * mm});
            skLineSegment(sketch, "E186.rect.right", {"start": v(-19.77, 10.08) * mm, "end": v(-19.77, 11.5) * mm});
            skPoint(sketch, "E186.rect.middle", {"position": v(-18.72, 10.79) * mm});
            skLineSegment(sketch, "E187.rect.bottom", {"start": v(-17.68, 15.73) * mm, "end": v(-19.77, 15.73) * mm});
            skLineSegment(sketch, "E187.rect.top", {"start": v(-17.68, 17.08) * mm, "end": v(-19.77, 17.08) * mm});
            skLineSegment(sketch, "E187.rect.left", {"start": v(-17.68, 15.73) * mm, "end": v(-17.68, 17.08) * mm});
            skLineSegment(sketch, "E187.rect.right", {"start": v(-19.77, 15.73) * mm, "end": v(-19.77, 17.08) * mm});
            skPoint(sketch, "E187.rect.middle", {"position": v(-18.72, 16.4) * mm});
            skLineSegment(sketch, "E188.rect.bottom", {"start": v(-11.68, 15.73) * mm, "end": v(-9.52, 15.73) * mm});
            skLineSegment(sketch, "E188.rect.top", {"start": v(-11.68, 17.08) * mm, "end": v(-9.52, 17.08) * mm});
            skLineSegment(sketch, "E188.rect.left", {"start": v(-11.68, 15.73) * mm, "end": v(-11.68, 17.08) * mm});
            skLineSegment(sketch, "E188.rect.right", {"start": v(-9.52, 15.73) * mm, "end": v(-9.52, 17.08) * mm});
            skPoint(sketch, "E188.rect.middle", {"position": v(-10.6, 16.4) * mm});
            skLineSegment(sketch, "E189.rect.bottom", {"start": v(-11.68, 10.02) * mm, "end": v(-9.52, 10.02) * mm});
            skLineSegment(sketch, "E189.rect.top", {"start": v(-11.68, 11.55) * mm, "end": v(-9.52, 11.55) * mm});
            skLineSegment(sketch, "E189.rect.left", {"start": v(-11.68, 10.02) * mm, "end": v(-11.68, 11.55) * mm});
            skLineSegment(sketch, "E189.rect.right", {"start": v(-9.52, 10.02) * mm, "end": v(-9.52, 11.55) * mm});
            skPoint(sketch, "E189.rect.middle", {"position": v(-10.6, 10.79) * mm});
            skLineSegment(sketch, "E190.rect.bottom", {"start": v(-9.5, 5.61) * mm, "end": v(-11.7, 5.61) * mm});
            skLineSegment(sketch, "E190.rect.top", {"start": v(-9.5, 4.23) * mm, "end": v(-11.7, 4.23) * mm});
            skLineSegment(sketch, "E190.rect.left", {"start": v(-9.5, 5.61) * mm, "end": v(-9.5, 4.23) * mm});
            skLineSegment(sketch, "E190.rect.right", {"start": v(-11.7, 5.61) * mm, "end": v(-11.7, 4.23) * mm});
            skPoint(sketch, "E190.rect.middle", {"position": v(-10.6, 4.92) * mm});
            skLineSegment(sketch, "E191.MirrorCS", {"start": v(2.26, 0.79) * mm, "end": v(2.26, 6.52) * mm});
            skLineSegment(sketch, "E192.MirrorCS", {"start": v(-0.8, 6.52) * mm, "end": v(2.26, 6.52) * mm});
            skLineSegment(sketch, "E193.MirrorCS", {"start": v(7.9, 5.61) * mm, "end": v(7.9, 4.23) * mm});
            skLineSegment(sketch, "E194.MirrorCS", {"start": v(7.9, 5.61) * mm, "end": v(10.09, 5.61) * mm});
            skLineSegment(sketch, "E195.MirrorCS", {"start": v(10.09, 5.61) * mm, "end": v(10.09, 4.23) * mm});
            skLineSegment(sketch, "E196.MirrorCS", {"start": v(7.9, 4.23) * mm, "end": v(10.09, 4.23) * mm});
            skLineSegment(sketch, "E197.MirrorCS", {"start": v(7.91, 10.02) * mm, "end": v(7.91, 11.55) * mm});
            skLineSegment(sketch, "E198.MirrorCS", {"start": v(10.08, 11.55) * mm, "end": v(7.91, 11.55) * mm});
            skLineSegment(sketch, "E199.MirrorCS", {"start": v(10.08, 10.02) * mm, "end": v(10.08, 11.55) * mm});
            skLineSegment(sketch, "E200.MirrorCS", {"start": v(10.08, 10.02) * mm, "end": v(7.91, 10.02) * mm});
            skLineSegment(sketch, "E201.MirrorCS", {"start": v(10.08, 17.08) * mm, "end": v(7.91, 17.08) * mm});
            skLineSegment(sketch, "E202.MirrorCS", {"start": v(7.91, 15.73) * mm, "end": v(7.91, 17.08) * mm});
            skLineSegment(sketch, "E203.MirrorCS", {"start": v(10.08, 15.73) * mm, "end": v(7.91, 15.73) * mm});
            skLineSegment(sketch, "E204.MirrorCS", {"start": v(10.08, 15.73) * mm, "end": v(10.08, 17.08) * mm});
            skLineSegment(sketch, "E205.MirrorCS", {"start": v(16.07, 15.73) * mm, "end": v(16.07, 17.08) * mm});
            skLineSegment(sketch, "E206.MirrorCS", {"start": v(16.07, 17.08) * mm, "end": v(18.16, 17.08) * mm});
            skLineSegment(sketch, "E207.MirrorCS", {"start": v(18.16, 15.73) * mm, "end": v(18.16, 17.08) * mm});
            skLineSegment(sketch, "E208.MirrorCS", {"start": v(16.07, 15.73) * mm, "end": v(18.16, 15.73) * mm});
            skLineSegment(sketch, "E209.MirrorCS", {"start": v(16.07, 11.5) * mm, "end": v(18.16, 11.5) * mm});
            skLineSegment(sketch, "E210.MirrorCS", {"start": v(16.07, 10.08) * mm, "end": v(16.07, 11.5) * mm});
            skLineSegment(sketch, "E211.MirrorCS", {"start": v(16.07, 10.08) * mm, "end": v(18.16, 10.08) * mm});
            skLineSegment(sketch, "E212.MirrorCS", {"start": v(18.16, 10.08) * mm, "end": v(18.16, 11.5) * mm});
            skLineSegment(sketch, "E213.MirrorCS", {"start": v(23.79, 15.86) * mm, "end": v(23.79, 16.95) * mm});
            skPoint(sketch, "E214.MirrorP", {"position": v(24.76, 16.4) * mm});
            skLineSegment(sketch, "E215.MirrorCS", {"start": v(23.79, 16.95) * mm, "end": v(25.73, 16.95) * mm});
            skLineSegment(sketch, "E216.MirrorCS", {"start": v(25.73, 15.86) * mm, "end": v(25.73, 16.95) * mm});
            skLineSegment(sketch, "E217.MirrorCS", {"start": v(23.79, 15.86) * mm, "end": v(25.73, 15.86) * mm});
            skLineSegment(sketch, "E218.MirrorCS", {"start": v(23.79, 11.44) * mm, "end": v(25.73, 11.44) * mm});
            skLineSegment(sketch, "E219.MirrorCS", {"start": v(23.79, 11.44) * mm, "end": v(23.79, 10.14) * mm});
            skLineSegment(sketch, "E220.MirrorCS", {"start": v(23.79, 10.14) * mm, "end": v(25.73, 10.14) * mm});
            skLineSegment(sketch, "E221.MirrorCS", {"start": v(25.73, 11.44) * mm, "end": v(25.73, 10.14) * mm});
            skPoint(sketch, "E222.MirrorP", {"position": v(24.76, 4.92) * mm});
            skPoint(sketch, "E223.MirrorP", {"position": v(17.12, 4.92) * mm});
            skPoint(sketch, "E224.MirrorP", {"position": v(9, 4.92) * mm});
            skPoint(sketch, "E225.MirrorP", {"position": v(9, 10.79) * mm});
            skPoint(sketch, "E226.MirrorP", {"position": v(9, 16.4) * mm});
            skPoint(sketch, "E227.MirrorP", {"position": v(17.12, 16.4) * mm});
            skPoint(sketch, "E228.MirrorP", {"position": v(17.12, 10.79) * mm});
            skPoint(sketch, "E229.MirrorP", {"position": v(24.76, 10.79) * mm});
            skLineSegment(sketch, "E230.MirrorCS", {"start": v(16.13, 5.61) * mm, "end": v(18.1, 5.61) * mm});
            skLineSegment(sketch, "E231.MirrorCS", {"start": v(18.1, 5.61) * mm, "end": v(18.1, 4.23) * mm});
            skLineSegment(sketch, "E232.MirrorCS", {"start": v(16.13, 4.23) * mm, "end": v(18.1, 4.23) * mm});
            skLineSegment(sketch, "E233.MirrorCS", {"start": v(16.13, 5.61) * mm, "end": v(16.13, 4.23) * mm});
            skLineSegment(sketch, "E234.MirrorCS", {"start": v(23.78, 5.61) * mm, "end": v(25.74, 5.61) * mm});
            skLineSegment(sketch, "E235.MirrorCS", {"start": v(25.74, 5.61) * mm, "end": v(25.74, 4.23) * mm});
            skLineSegment(sketch, "E236.MirrorCS", {"start": v(23.78, 4.23) * mm, "end": v(25.74, 4.23) * mm});
            skLineSegment(sketch, "E237.MirrorCS", {"start": v(23.78, 5.61) * mm, "end": v(23.78, 4.23) * mm});
            skLineSegment(sketch, "E238", {"start": v(2.26, 0.79) * mm, "end": v(-0.8, 0.79) * mm});
            skSolve(sketch);
        }
        {
            var Q0;
            Q0=makeQuery(id+"F1.opExtrude","SWEPT_FACE",FACE,{"disambiguationData":[OSD([sQuery(id+"F0.wireOp",EDGE,"E3.4")])]});
            var sketch = newSketch(context, id + "F10", { "sketchPlane" : qUnion([Q0])});
            skLineSegment(sketch, "E239.bottom", {"start": v(-0.8, 0.79) * mm, "end": v(-3.87, 0.79) * mm});
            skLineSegment(sketch, "E239.top", {"start": v(-0.8, 6.52) * mm, "end": v(-3.87, 6.52) * mm});
            skLineSegment(sketch, "E239.left", {"start": v(-0.8, 0.79) * mm, "end": v(-0.8, 6.52) * mm});
            skLineSegment(sketch, "E239.right", {"start": v(-3.87, 0.79) * mm, "end": v(-3.87, 6.52) * mm});
            skLineSegment(sketch, "E240.rect.bottom", {"start": v(-25.4, 15.86) * mm, "end": v(-27.33, 15.86) * mm});
            skLineSegment(sketch, "E240.rect.top", {"start": v(-25.4, 16.95) * mm, "end": v(-27.33, 16.95) * mm});
            skLineSegment(sketch, "E240.rect.left", {"start": v(-25.4, 15.86) * mm, "end": v(-25.4, 16.95) * mm});
            skLineSegment(sketch, "E240.rect.right", {"start": v(-27.33, 15.86) * mm, "end": v(-27.33, 16.95) * mm});
            skPoint(sketch, "E240.rect.middle", {"position": v(-26.36, 16.4) * mm});
            skLineSegment(sketch, "E241.rect.bottom", {"start": v(-25.4, 11.44) * mm, "end": v(-27.33, 11.44) * mm});
            skLineSegment(sketch, "E241.rect.top", {"start": v(-25.4, 10.14) * mm, "end": v(-27.33, 10.14) * mm});
            skLineSegment(sketch, "E241.rect.left", {"start": v(-25.4, 11.44) * mm, "end": v(-25.4, 10.14) * mm});
            skLineSegment(sketch, "E241.rect.right", {"start": v(-27.33, 11.44) * mm, "end": v(-27.33, 10.14) * mm});
            skPoint(sketch, "E241.rect.middle", {"position": v(-26.36, 10.79) * mm});
            skLineSegment(sketch, "E242.rect.bottom", {"start": v(-25.38, 5.61) * mm, "end": v(-27.34, 5.61) * mm});
            skLineSegment(sketch, "E242.rect.top", {"start": v(-25.38, 4.23) * mm, "end": v(-27.34, 4.23) * mm});
            skLineSegment(sketch, "E242.rect.left", {"start": v(-25.38, 5.61) * mm, "end": v(-25.38, 4.23) * mm});
            skLineSegment(sketch, "E242.rect.right", {"start": v(-27.34, 5.61) * mm, "end": v(-27.34, 4.23) * mm});
            skPoint(sketch, "E242.rect.middle", {"position": v(-26.36, 4.92) * mm});
            skLineSegment(sketch, "E243.rect.bottom", {"start": v(-17.74, 5.61) * mm, "end": v(-19.71, 5.61) * mm});
            skLineSegment(sketch, "E243.rect.top", {"start": v(-17.74, 4.23) * mm, "end": v(-19.71, 4.23) * mm});
            skLineSegment(sketch, "E243.rect.left", {"start": v(-17.74, 5.61) * mm, "end": v(-17.74, 4.23) * mm});
            skLineSegment(sketch, "E243.rect.right", {"start": v(-19.71, 5.61) * mm, "end": v(-19.71, 4.23) * mm});
            skPoint(sketch, "E243.rect.middle", {"position": v(-18.72, 4.92) * mm});
            skLineSegment(sketch, "E244.rect.bottom", {"start": v(-17.68, 10.08) * mm, "end": v(-19.77, 10.08) * mm});
            skLineSegment(sketch, "E244.rect.top", {"start": v(-17.68, 11.5) * mm, "end": v(-19.77, 11.5) * mm});
            skLineSegment(sketch, "E244.rect.left", {"start": v(-17.68, 10.08) * mm, "end": v(-17.68, 11.5) * mm});
            skLineSegment(sketch, "E244.rect.right", {"start": v(-19.77, 10.08) * mm, "end": v(-19.77, 11.5) * mm});
            skPoint(sketch, "E244.rect.middle", {"position": v(-18.72, 10.79) * mm});
            skLineSegment(sketch, "E245.rect.bottom", {"start": v(-17.68, 15.73) * mm, "end": v(-19.77, 15.73) * mm});
            skLineSegment(sketch, "E245.rect.top", {"start": v(-17.68, 17.08) * mm, "end": v(-19.77, 17.08) * mm});
            skLineSegment(sketch, "E245.rect.left", {"start": v(-17.68, 15.73) * mm, "end": v(-17.68, 17.08) * mm});
            skLineSegment(sketch, "E245.rect.right", {"start": v(-19.77, 15.73) * mm, "end": v(-19.77, 17.08) * mm});
            skPoint(sketch, "E245.rect.middle", {"position": v(-18.72, 16.4) * mm});
            skLineSegment(sketch, "E246.rect.bottom", {"start": v(-11.68, 15.73) * mm, "end": v(-9.52, 15.73) * mm});
            skLineSegment(sketch, "E246.rect.top", {"start": v(-11.68, 17.08) * mm, "end": v(-9.52, 17.08) * mm});
            skLineSegment(sketch, "E246.rect.left", {"start": v(-11.68, 15.73) * mm, "end": v(-11.68, 17.08) * mm});
            skLineSegment(sketch, "E246.rect.right", {"start": v(-9.52, 15.73) * mm, "end": v(-9.52, 17.08) * mm});
            skPoint(sketch, "E246.rect.middle", {"position": v(-10.6, 16.4) * mm});
            skLineSegment(sketch, "E247.rect.bottom", {"start": v(-11.68, 10.02) * mm, "end": v(-9.52, 10.02) * mm});
            skLineSegment(sketch, "E247.rect.top", {"start": v(-11.68, 11.55) * mm, "end": v(-9.52, 11.55) * mm});
            skLineSegment(sketch, "E247.rect.left", {"start": v(-11.68, 10.02) * mm, "end": v(-11.68, 11.55) * mm});
            skLineSegment(sketch, "E247.rect.right", {"start": v(-9.52, 10.02) * mm, "end": v(-9.52, 11.55) * mm});
            skPoint(sketch, "E247.rect.middle", {"position": v(-10.6, 10.79) * mm});
            skLineSegment(sketch, "E248.rect.bottom", {"start": v(-9.5, 5.61) * mm, "end": v(-11.7, 5.61) * mm});
            skLineSegment(sketch, "E248.rect.top", {"start": v(-9.5, 4.23) * mm, "end": v(-11.7, 4.23) * mm});
            skLineSegment(sketch, "E248.rect.left", {"start": v(-9.5, 5.61) * mm, "end": v(-9.5, 4.23) * mm});
            skLineSegment(sketch, "E248.rect.right", {"start": v(-11.7, 5.61) * mm, "end": v(-11.7, 4.23) * mm});
            skPoint(sketch, "E248.rect.middle", {"position": v(-10.6, 4.92) * mm});
            skLineSegment(sketch, "E249.MirrorCS", {"start": v(2.26, 0.79) * mm, "end": v(2.26, 6.52) * mm});
            skLineSegment(sketch, "E250.MirrorCS", {"start": v(-0.8, 6.52) * mm, "end": v(2.26, 6.52) * mm});
            skLineSegment(sketch, "E251.MirrorCS", {"start": v(7.9, 5.61) * mm, "end": v(7.9, 4.23) * mm});
            skLineSegment(sketch, "E252.MirrorCS", {"start": v(7.9, 5.61) * mm, "end": v(10.09, 5.61) * mm});
            skLineSegment(sketch, "E253.MirrorCS", {"start": v(10.09, 5.61) * mm, "end": v(10.09, 4.23) * mm});
            skLineSegment(sketch, "E254.MirrorCS", {"start": v(7.9, 4.23) * mm, "end": v(10.09, 4.23) * mm});
            skLineSegment(sketch, "E255.MirrorCS", {"start": v(7.91, 10.02) * mm, "end": v(7.91, 11.55) * mm});
            skLineSegment(sketch, "E256.MirrorCS", {"start": v(10.08, 11.55) * mm, "end": v(7.91, 11.55) * mm});
            skLineSegment(sketch, "E257.MirrorCS", {"start": v(10.08, 10.02) * mm, "end": v(10.08, 11.55) * mm});
            skLineSegment(sketch, "E258.MirrorCS", {"start": v(10.08, 10.02) * mm, "end": v(7.91, 10.02) * mm});
            skLineSegment(sketch, "E259.MirrorCS", {"start": v(10.08, 17.08) * mm, "end": v(7.91, 17.08) * mm});
            skLineSegment(sketch, "E260.MirrorCS", {"start": v(7.91, 15.73) * mm, "end": v(7.91, 17.08) * mm});
            skLineSegment(sketch, "E261.MirrorCS", {"start": v(10.08, 15.73) * mm, "end": v(7.91, 15.73) * mm});
            skLineSegment(sketch, "E262.MirrorCS", {"start": v(10.08, 15.73) * mm, "end": v(10.08, 17.08) * mm});
            skLineSegment(sketch, "E263.MirrorCS", {"start": v(16.07, 15.73) * mm, "end": v(16.07, 17.08) * mm});
            skLineSegment(sketch, "E264.MirrorCS", {"start": v(16.07, 17.08) * mm, "end": v(18.16, 17.08) * mm});
            skLineSegment(sketch, "E265.MirrorCS", {"start": v(18.16, 15.73) * mm, "end": v(18.16, 17.08) * mm});
            skLineSegment(sketch, "E266.MirrorCS", {"start": v(16.07, 15.73) * mm, "end": v(18.16, 15.73) * mm});
            skLineSegment(sketch, "E267.MirrorCS", {"start": v(16.07, 11.5) * mm, "end": v(18.16, 11.5) * mm});
            skLineSegment(sketch, "E268.MirrorCS", {"start": v(16.07, 10.08) * mm, "end": v(16.07, 11.5) * mm});
            skLineSegment(sketch, "E269.MirrorCS", {"start": v(16.07, 10.08) * mm, "end": v(18.16, 10.08) * mm});
            skLineSegment(sketch, "E270.MirrorCS", {"start": v(18.16, 10.08) * mm, "end": v(18.16, 11.5) * mm});
            skLineSegment(sketch, "E271.MirrorCS", {"start": v(23.79, 15.86) * mm, "end": v(23.79, 16.95) * mm});
            skPoint(sketch, "E272.MirrorP", {"position": v(24.76, 16.4) * mm});
            skLineSegment(sketch, "E273.MirrorCS", {"start": v(23.79, 16.95) * mm, "end": v(25.73, 16.95) * mm});
            skLineSegment(sketch, "E274.MirrorCS", {"start": v(25.73, 15.86) * mm, "end": v(25.73, 16.95) * mm});
            skLineSegment(sketch, "E275.MirrorCS", {"start": v(23.79, 15.86) * mm, "end": v(25.73, 15.86) * mm});
            skLineSegment(sketch, "E276.MirrorCS", {"start": v(23.79, 11.44) * mm, "end": v(25.73, 11.44) * mm});
            skLineSegment(sketch, "E277.MirrorCS", {"start": v(23.79, 11.44) * mm, "end": v(23.79, 10.14) * mm});
            skLineSegment(sketch, "E278.MirrorCS", {"start": v(23.79, 10.14) * mm, "end": v(25.73, 10.14) * mm});
            skLineSegment(sketch, "E279.MirrorCS", {"start": v(25.73, 11.44) * mm, "end": v(25.73, 10.14) * mm});
            skPoint(sketch, "E280.MirrorP", {"position": v(24.76, 4.92) * mm});
            skPoint(sketch, "E281.MirrorP", {"position": v(17.12, 4.92) * mm});
            skPoint(sketch, "E282.MirrorP", {"position": v(9, 4.92) * mm});
            skPoint(sketch, "E283.MirrorP", {"position": v(9, 10.79) * mm});
            skPoint(sketch, "E284.MirrorP", {"position": v(9, 16.4) * mm});
            skPoint(sketch, "E285.MirrorP", {"position": v(17.12, 16.4) * mm});
            skPoint(sketch, "E286.MirrorP", {"position": v(17.12, 10.79) * mm});
            skPoint(sketch, "E287.MirrorP", {"position": v(24.76, 10.79) * mm});
            skLineSegment(sketch, "E288.MirrorCS", {"start": v(16.13, 5.61) * mm, "end": v(18.1, 5.61) * mm});
            skLineSegment(sketch, "E289.MirrorCS", {"start": v(18.1, 5.61) * mm, "end": v(18.1, 4.23) * mm});
            skLineSegment(sketch, "E290.MirrorCS", {"start": v(16.13, 4.23) * mm, "end": v(18.1, 4.23) * mm});
            skLineSegment(sketch, "E291.MirrorCS", {"start": v(16.13, 5.61) * mm, "end": v(16.13, 4.23) * mm});
            skLineSegment(sketch, "E292.MirrorCS", {"start": v(23.78, 5.61) * mm, "end": v(25.74, 5.61) * mm});
            skLineSegment(sketch, "E293.MirrorCS", {"start": v(25.74, 5.61) * mm, "end": v(25.74, 4.23) * mm});
            skLineSegment(sketch, "E294.MirrorCS", {"start": v(23.78, 4.23) * mm, "end": v(25.74, 4.23) * mm});
            skLineSegment(sketch, "E295.MirrorCS", {"start": v(23.78, 5.61) * mm, "end": v(23.78, 4.23) * mm});
            skLineSegment(sketch, "E296", {"start": v(2.26, 0.79) * mm, "end": v(-0.8, 0.79) * mm});
            skSolve(sketch);
        }
        {
            var Q0;
            Q0 = qSketchRegion(id + "F7", true);
            extrude(context, id + "F11", {"entities" : qUnion([Q0]), "operationType" : NewBodyOperationType.REMOVE, "oppositeDirection" : true, "depth" : 32.3 * mm});
        }
        {
            var Q0;
            Q0 = qSketchRegion(id + "F8", true);
            extrude(context, id + "F12", {"entities" : qUnion([Q0]), "operationType" : NewBodyOperationType.REMOVE, "oppositeDirection" : true, "depth" : 22.18 * mm});
        }
        {
            var Q0;
            Q0 = qSketchRegion(id + "F9", true);
            extrude(context, id + "F13", {"entities" : qUnion([Q0]), "operationType" : NewBodyOperationType.REMOVE, "oppositeDirection" : true, "depth" : 25 * mm});
        }
        {
            var Q0;
            Q0 = qSketchRegion(id + "F10", true);
            extrude(context, id + "F14", {"entities" : qUnion([Q0]), "operationType" : NewBodyOperationType.REMOVE, "oppositeDirection" : true, "depth" : 25 * mm});
        }
        {
            var Q0;
            Q0=makeQuery(id+"F1.opExtrude","CAP_FACE",FACE,{"disambiguationData":[OSD([sQuery(id+"F0.wireOp",EDGE,"E1.0"),sQuery(id+"F0.wireOp",EDGE,"E1.1"),sQuery(id+"F0.wireOp",EDGE,"E1.2"),sQuery(id+"F0.wireOp",EDGE,"E1.3"),sQuery(id+"F0.wireOp",EDGE,"E1.4"),sQuery(id+"F0.wireOp",EDGE,"E2.0"),sQuery(id+"F0.wireOp",EDGE,"E2.1"),sQuery(id+"F0.wireOp",EDGE,"E2.2"),sQuery(id+"F0.wireOp",EDGE,"E2.3"),sQuery(id+"F0.wireOp",EDGE,"E2.4")])],"isStart":true});
            var sketch = newSketch(context, id + "F15", { "sketchPlane" : qUnion([Q0])});
            skLineSegment(sketch, "E297.rect.bottom", {"start": v(49.5, 49.5) * mm, "end": v(-49.5, 49.5) * mm});
            skLineSegment(sketch, "E297.rect.top", {"start": v(49.5, -49.5) * mm, "end": v(-49.5, -49.5) * mm});
            skLineSegment(sketch, "E297.rect.left", {"start": v(49.5, 49.5) * mm, "end": v(49.5, -49.5) * mm});
            skLineSegment(sketch, "E297.rect.right", {"start": v(-49.5, 49.5) * mm, "end": v(-49.5, -49.5) * mm});
            skPoint(sketch, "E297.rect.middle", {"position": v(0, 0) * mm});
            skSolve(sketch);
        }
        {
            var Q0;
            Q0 = qSketchRegion(id + "F15", true);
            extrude(context, id + "F16", {"entities" : qUnion([Q0]), "depth" : 1.5 * mm});
        }
        {
            var Q0;
            Q0=makeQuery(id+"F1.opExtrude","CAP_EDGE",EDGE,{"disambiguationData":[OSD([sQuery(id+"F0.wireOp",EDGE,"E3.3")])],"isStart":false});
            var Q1;
            Q1=makeQuery(id+"F1.opExtrude","CAP_EDGE",EDGE,{"disambiguationData":[OSD([sQuery(id+"F0.wireOp",EDGE,"E3.4")])],"isStart":false});
            var Q2;
            Q2=makeQuery(id+"F1.opExtrude","CAP_EDGE",EDGE,{"disambiguationData":[OSD([sQuery(id+"F0.wireOp",EDGE,"E0.4")])],"isStart":false});
            var Q3;
            Q3=makeQuery(id+"F1.opExtrude","CAP_EDGE",EDGE,{"disambiguationData":[OSD([sQuery(id+"F0.wireOp",EDGE,"E0.3")])],"isStart":false});
            var Q4;
            Q4=makeQuery(id+"F1.opExtrude","CAP_EDGE",EDGE,{"disambiguationData":[OSD([sQuery(id+"F0.wireOp",EDGE,"E1.4")])],"isStart":false});
            var Q5;
            Q5=makeQuery(id+"F1.opExtrude","CAP_EDGE",EDGE,{"disambiguationData":[OSD([sQuery(id+"F0.wireOp",EDGE,"E2.4")])],"isStart":false});
            var Q6;
            Q6=makeQuery(id+"F1.opExtrude","CAP_EDGE",EDGE,{"disambiguationData":[OSD([sQuery(id+"F0.wireOp",EDGE,"E2.3")])],"isStart":false});
            var Q7;
            Q7=makeQuery(id+"F1.opExtrude","CAP_EDGE",EDGE,{"disambiguationData":[OSD([sQuery(id+"F0.wireOp",EDGE,"E1.3")])],"isStart":false});
            var Q8;
            Q8=makeQuery(id+"F1.opExtrude","CAP_EDGE",EDGE,{"disambiguationData":[OSD([sQuery(id+"F0.wireOp",EDGE,"E2.0")])],"isStart":false});
            var Q9;
            Q9=makeQuery(id+"F1.opExtrude","CAP_EDGE",EDGE,{"disambiguationData":[OSD([sQuery(id+"F0.wireOp",EDGE,"E1.0")])],"isStart":false});
            var Q10;
            Q10=makeQuery(id+"F1.opExtrude","CAP_EDGE",EDGE,{"disambiguationData":[OSD([sQuery(id+"F0.wireOp",EDGE,"E0.0")])],"isStart":false});
            var Q11;
            Q11=makeQuery(id+"F1.opExtrude","CAP_EDGE",EDGE,{"disambiguationData":[OSD([sQuery(id+"F0.wireOp",EDGE,"E3.0")])],"isStart":false});
            var Q12;
            Q12=makeQuery(id+"F1.opExtrude","CAP_EDGE",EDGE,{"disambiguationData":[OSD([sQuery(id+"F0.wireOp",EDGE,"E1.2")])],"isStart":false});
            var Q13;
            Q13=makeQuery(id+"F1.opExtrude","CAP_EDGE",EDGE,{"disambiguationData":[OSD([sQuery(id+"F0.wireOp",EDGE,"E2.2")])],"isStart":false});
            var Q14;
            Q14=makeQuery(id+"F1.opExtrude","CAP_EDGE",EDGE,{"disambiguationData":[OSD([sQuery(id+"F0.wireOp",EDGE,"E2.1")])],"isStart":false});
            var Q15;
            Q15=makeQuery(id+"F1.opExtrude","CAP_EDGE",EDGE,{"disambiguationData":[OSD([sQuery(id+"F0.wireOp",EDGE,"E1.1")])],"isStart":false});
            var Q16;
            Q16=makeQuery(id+"F1.opExtrude","CAP_EDGE",EDGE,{"disambiguationData":[OSD([sQuery(id+"F0.wireOp",EDGE,"E0.1")])],"isStart":false});
            var Q17;
            Q17=makeQuery(id+"F1.opExtrude","CAP_EDGE",EDGE,{"disambiguationData":[OSD([sQuery(id+"F0.wireOp",EDGE,"E3.1")])],"isStart":false});
            var Q18;
            Q18=makeQuery(id+"F1.opExtrude","CAP_EDGE",EDGE,{"disambiguationData":[OSD([sQuery(id+"F0.wireOp",EDGE,"E3.2")])],"isStart":false});
            var Q19;
            Q19=makeQuery(id+"F1.opExtrude","CAP_EDGE",EDGE,{"disambiguationData":[OSD([sQuery(id+"F0.wireOp",EDGE,"E0.2")])],"isStart":false});
            fillet(context, id + "F17", {"entities" : qUnion([Q0, Q1, Q2, Q3, Q4, Q5, Q6, Q7, Q8, Q9, Q10, Q11, Q12, Q13, Q14, Q15, Q16, Q17, Q18, Q19]), "radius" : 2 * mm, "tangentPropagation" : true, "allowEdgeOverflow" : false});
        }
    });
